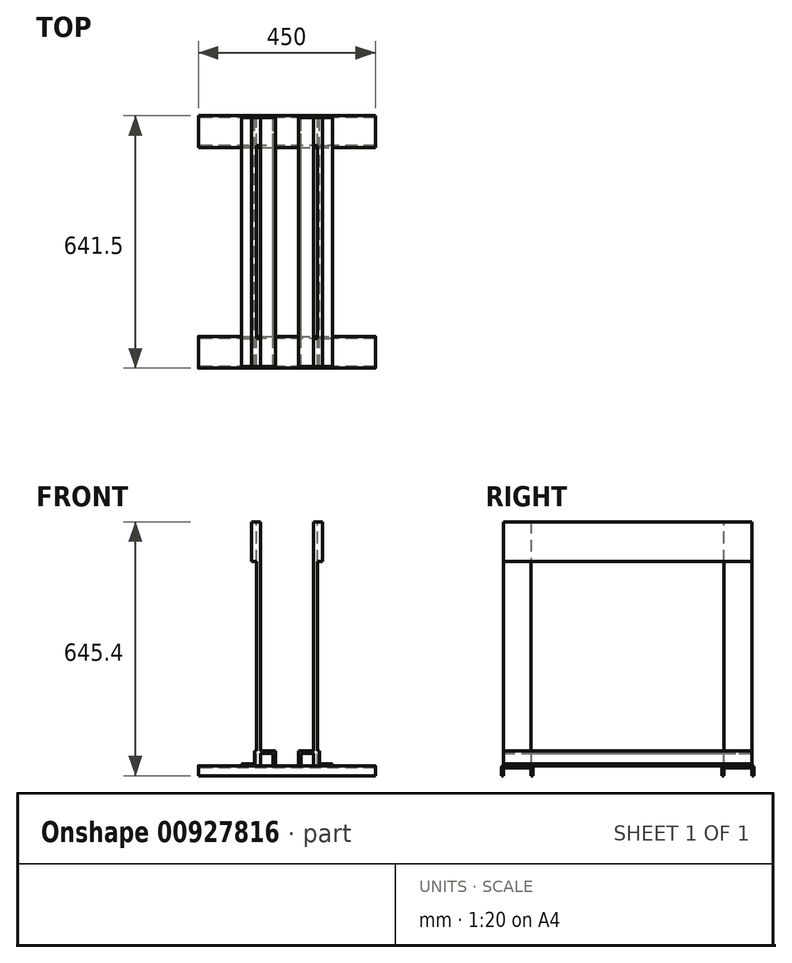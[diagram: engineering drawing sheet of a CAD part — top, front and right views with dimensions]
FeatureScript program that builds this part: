
annotation { "Feature Type Name" : "Feature", "Feature Type Description" : "" }
export const myFeature = defineFeature(function(context is Context, id is Id, definition is map)
    precondition{}
    {
        {
            var Q0;
            Q0=qCreatedBy(makeId("Front.planeOp"),FACE);
            var sketch = newSketch(context, id + "F0", { "sketchPlane" : qUnion([Q0])});
            skLineSegment(sketch, "E0.bottom", {"start": v(0, 0) * mm, "end": v(-10.45, 0) * mm});
            skLineSegment(sketch, "E0.top", {"start": v(0, 620) * mm, "end": v(-10.45, 620) * mm});
            skLineSegment(sketch, "E0.left", {"start": v(0, 0) * mm, "end": v(0, 620) * mm});
            skLineSegment(sketch, "E0.right", {"start": v(-10.45, 0) * mm, "end": v(-10.45, 620) * mm});
            skLineSegment(sketch, "E1", {"start": v(0, 38.1) * mm, "end": v(38.1, 38.1) * mm});
            skLineSegment(sketch, "E2", {"start": v(38.1, 38.1) * mm, "end": v(38.1, 0) * mm});
            skLineSegment(sketch, "E3", {"start": v(38.1, 0) * mm, "end": v(31.75, 0) * mm});
            skLineSegment(sketch, "E4", {"start": v(31.75, 0) * mm, "end": v(31.75, 31.75) * mm});
            skLineSegment(sketch, "E5", {"start": v(31.75, 31.75) * mm, "end": v(0, 31.75) * mm});
            skSolve(sketch);
        }
        {
            var Q0;
            {var subQ0=sQuery(id+"F0.wireOp",EDGE,"E1");Q0=makeQuery(id+"F0.imprint","IMPRINT",FACE,{"disambiguationData":[TD([[makeQuery(id+"F0.imprint","IMPRINT",EDGE,{"derivedFrom":subQ0}),-1.0]])]});}
            extrude(context, id + "F1", {"entities" : qUnion([Q0]), "depth" : 631.5 * mm, "offsetDistance" : 25 * mm});
        }
        {
            var Q0;
            {var subQ3=sQuery(id+"F0.wireOp",EDGE,"E0.bottom");Q0=makeQuery(id+"F0.imprint","IMPRINT",FACE,{"disambiguationData":[TD([[makeQuery(id+"F0.imprint","IMPRINT",EDGE,{"derivedFrom":subQ3}),-1.0]])]});}
            extrude(context, id + "F2", {"entities" : qUnion([Q0]), "operationType" : NewBodyOperationType.ADD, "depth" : 70.75 * mm, "offsetDistance" : 25 * mm});
        }
        {
            var Q0;
            Q0=qCreatedBy(makeId("Top.planeOp"),FACE);
            var sketch = newSketch(context, id + "F3", { "sketchPlane" : qUnion([Q0])});
            skLineSegment(sketch, "E6.bottom", {"start": v(0, -631.5) * mm, "end": v(-10.45, -631.5) * mm});
            skLineSegment(sketch, "E6.top", {"start": v(0, -560.75) * mm, "end": v(-10.45, -560.75) * mm});
            skLineSegment(sketch, "E6.left", {"start": v(0, -631.5) * mm, "end": v(0, -560.75) * mm});
            skLineSegment(sketch, "E6.right", {"start": v(-10.45, -631.5) * mm, "end": v(-10.45, -560.75) * mm});
            skSolve(sketch);
        }
        {
            var Q0;
            Q0=qSketchRegion(id+"F3",true);
            extrude(context, id + "F4", {"entities" : qUnion([Q0]), "operationType" : NewBodyOperationType.ADD, "depth" : 620 * mm, "offsetDistance" : 25 * mm});
        }
        {
            var Q0;
            Q0=qCreatedBy(makeId("Top.planeOp"),FACE);
            var sketch = newSketch(context, id + "F5", { "sketchPlane" : qUnion([Q0])});
            skLineSegment(sketch, "E7.bottom", {"start": v(-157.8, 5) * mm, "end": v(292.2, 5) * mm});
            skLineSegment(sketch, "E7.top", {"start": v(-157.8, -75.75) * mm, "end": v(292.2, -75.75) * mm});
            skLineSegment(sketch, "E7.left", {"start": v(-157.8, 5) * mm, "end": v(-157.8, -75.75) * mm});
            skLineSegment(sketch, "E7.right", {"start": v(292.2, 5) * mm, "end": v(292.2, -75.75) * mm});
            skLineSegment(sketch, "E8.bottom", {"start": v(-157.8, -636.5) * mm, "end": v(292.2, -636.5) * mm});
            skLineSegment(sketch, "E8.top", {"start": v(-157.8, -555.75) * mm, "end": v(292.2, -555.75) * mm});
            skLineSegment(sketch, "E8.left", {"start": v(-157.8, -636.5) * mm, "end": v(-157.8, -555.75) * mm});
            skLineSegment(sketch, "E8.right", {"start": v(292.2, -636.5) * mm, "end": v(292.2, -555.75) * mm});
            skSolve(sketch);
        }
        {
            var Q0;
            Q0=qSketchRegion(id+"F5",true);
            extrude(context, id + "F6", {"entities" : qUnion([Q0]), "operationType" : NewBodyOperationType.ADD, "oppositeDirection" : true, "depth" : 25.4 * mm, "offsetDistance" : 25 * mm});
        }
        {
            var Q0;
            Q0=makeQuery(id+"F6.opExtrude","CAP_EDGE",EDGE,{"disambiguationData":[OSD([sQuery(id+"F5.wireOp",EDGE,"E8.bottom")])],"isStart":true});
            var Q1;
            {var subQ0=sQuery(id+"F5.wireOp",EDGE,"E8.top");var subQ1=makeQuery(id+"F6.opExtrude","SWEPT_FACE",FACE,{"disambiguationData":[OSD([subQ0])]});var subQ2=sQuery(id+"F5.wireOp",EDGE,"E8.right");var subQ3=makeQuery(id+"F6.opExtrude","CAP_FACE",FACE,{"disambiguationData":[OSD([sQuery(id+"F5.wireOp",EDGE,"E8.bottom"),subQ0,sQuery(id+"F5.wireOp",EDGE,"E8.left"),subQ2])],"isStart":true});Q1=makeQuery(id+"F6.boolean.opBoolean","SPLIT",EDGE,{"disambiguationData":[topologyDisambiguationEdgeConnected([subQ3,subQ1]),TD([makeQuery(id+"F1.opExtrude","SWEPT_FACE",FACE,{"disambiguationData":[OSD([sQuery(id+"F0.wireOp",EDGE,"E2")])]})])],"derivedFrom":makeQuery(id+"F6.opExtrude","CAP_EDGE",EDGE,{"disambiguationData":[OSD([subQ0])],"isStart":true})});}
            var Q2;
            {var subQ0=sQuery(id+"F5.wireOp",EDGE,"E8.top");var subQ1=makeQuery(id+"F6.opExtrude","SWEPT_FACE",FACE,{"disambiguationData":[OSD([subQ0])]});var subQ2=sQuery(id+"F5.wireOp",EDGE,"E8.left");var subQ3=makeQuery(id+"F6.opExtrude","CAP_FACE",FACE,{"disambiguationData":[OSD([sQuery(id+"F5.wireOp",EDGE,"E8.bottom"),subQ0,subQ2,sQuery(id+"F5.wireOp",EDGE,"E8.right")])],"isStart":true});Q2=makeQuery(id+"F6.boolean.opBoolean","SPLIT",EDGE,{"disambiguationData":[topologyDisambiguationEdgeConnected([subQ3,subQ1]),TD([makeQuery(id+"F1.opExtrude","SWEPT_FACE",FACE,{"disambiguationData":[OSD([sQuery(id+"F0.wireOp",EDGE,"E4")])]})])],"derivedFrom":makeQuery(id+"F6.opExtrude","CAP_EDGE",EDGE,{"disambiguationData":[OSD([subQ0])],"isStart":true})});}
            var Q3;
            {var subQ0=sQuery(id+"F5.wireOp",EDGE,"E7.top");var subQ1=makeQuery(id+"F6.opExtrude","SWEPT_FACE",FACE,{"disambiguationData":[OSD([subQ0])]});var subQ2=sQuery(id+"F5.wireOp",EDGE,"E7.right");var subQ3=makeQuery(id+"F6.opExtrude","CAP_FACE",FACE,{"disambiguationData":[OSD([sQuery(id+"F5.wireOp",EDGE,"E7.bottom"),subQ0,sQuery(id+"F5.wireOp",EDGE,"E7.left"),subQ2])],"isStart":true});Q3=makeQuery(id+"F6.boolean.opBoolean","SPLIT",EDGE,{"disambiguationData":[topologyDisambiguationEdgeConnected([subQ3,subQ1]),TD([makeQuery(id+"F1.opExtrude","SWEPT_FACE",FACE,{"disambiguationData":[OSD([sQuery(id+"F0.wireOp",EDGE,"E2")])]})])],"derivedFrom":makeQuery(id+"F6.opExtrude","CAP_EDGE",EDGE,{"disambiguationData":[OSD([subQ0])],"isStart":true})});}
            var Q4;
            {var subQ0=sQuery(id+"F5.wireOp",EDGE,"E7.top");var subQ1=makeQuery(id+"F6.opExtrude","SWEPT_FACE",FACE,{"disambiguationData":[OSD([subQ0])]});var subQ2=sQuery(id+"F5.wireOp",EDGE,"E7.left");var subQ3=makeQuery(id+"F6.opExtrude","CAP_FACE",FACE,{"disambiguationData":[OSD([sQuery(id+"F5.wireOp",EDGE,"E7.bottom"),subQ0,subQ2,sQuery(id+"F5.wireOp",EDGE,"E7.right")])],"isStart":true});Q4=makeQuery(id+"F6.boolean.opBoolean","SPLIT",EDGE,{"disambiguationData":[topologyDisambiguationEdgeConnected([subQ3,subQ1]),TD([makeQuery(id+"F1.opExtrude","SWEPT_FACE",FACE,{"disambiguationData":[OSD([sQuery(id+"F0.wireOp",EDGE,"E4")])]})])],"derivedFrom":makeQuery(id+"F6.opExtrude","CAP_EDGE",EDGE,{"disambiguationData":[OSD([subQ0])],"isStart":true})});}
            var Q5;
            Q5=makeQuery(id+"F6.opExtrude","CAP_EDGE",EDGE,{"disambiguationData":[OSD([sQuery(id+"F5.wireOp",EDGE,"E7.bottom")])],"isStart":true});
            fillet(context, id + "F7", {"entities" : qUnion([Q0, Q1, Q2, Q3, Q4, Q5]), "radius" : 5 * mm, "tangentPropagation" : true, "allowEdgeOverflow" : false});
        }
        {
            var Q0;
            Q0=qCreatedBy(makeId("Front.planeOp"),FACE);
            var sketch = newSketch(context, id + "F8", { "sketchPlane" : qUnion([Q0])});
            skLineSegment(sketch, "E9.bottom", {"start": v(134.4, 0) * mm, "end": v(144.85, 0) * mm});
            skLineSegment(sketch, "E9.top", {"start": v(134.4, 620) * mm, "end": v(144.85, 620) * mm});
            skLineSegment(sketch, "E9.left", {"start": v(134.4, 0) * mm, "end": v(134.4, 620) * mm});
            skLineSegment(sketch, "E9.right", {"start": v(144.85, 0) * mm, "end": v(144.85, 620) * mm});
            skLineSegment(sketch, "E10", {"start": v(134.4, 38.1) * mm, "end": v(96.3, 38.1) * mm});
            skLineSegment(sketch, "E11", {"start": v(96.3, 38.1) * mm, "end": v(96.3, 0) * mm});
            skLineSegment(sketch, "E12", {"start": v(96.3, 0) * mm, "end": v(102.65, 0) * mm});
            skLineSegment(sketch, "E13", {"start": v(102.65, 0) * mm, "end": v(102.65, 31.75) * mm});
            skLineSegment(sketch, "E14", {"start": v(102.65, 31.75) * mm, "end": v(134.4, 31.75) * mm});
            skSolve(sketch);
        }
        {
            var Q0;
            {var subQ0=sQuery(id+"F8.wireOp",EDGE,"E10");Q0=makeQuery(id+"F8.imprint","IMPRINT",FACE,{"disambiguationData":[TD([[makeQuery(id+"F8.imprint","IMPRINT",EDGE,{"derivedFrom":subQ0}),1.0]])]});}
            extrude(context, id + "F9", {"entities" : qUnion([Q0]), "operationType" : NewBodyOperationType.ADD, "depth" : 631.5 * mm, "offsetDistance" : 25 * mm});
        }
        {
            var Q0;
            Q0=qSketchRegion(id+"F8",true);
            extrude(context, id + "F10", {"entities" : qUnion([Q0]), "operationType" : NewBodyOperationType.ADD, "depth" : 70.75 * mm, "offsetDistance" : 25 * mm});
        }
        {
            var Q0;
            Q0=qCreatedBy(makeId("Top.planeOp"),FACE);
            var sketch = newSketch(context, id + "F11", { "sketchPlane" : qUnion([Q0])});
            skLineSegment(sketch, "E15.bottom", {"start": v(134.4, -631.5) * mm, "end": v(144.85, -631.5) * mm});
            skLineSegment(sketch, "E15.top", {"start": v(134.4, -560.75) * mm, "end": v(144.85, -560.75) * mm});
            skLineSegment(sketch, "E15.left", {"start": v(134.4, -631.5) * mm, "end": v(134.4, -560.75) * mm});
            skLineSegment(sketch, "E15.right", {"start": v(144.85, -631.5) * mm, "end": v(144.85, -560.75) * mm});
            skSolve(sketch);
        }
        {
            var Q0;
            Q0=qSketchRegion(id+"F11",true);
            extrude(context, id + "F12", {"entities" : qUnion([Q0]), "operationType" : NewBodyOperationType.ADD, "depth" : 620 * mm, "offsetDistance" : 25 * mm});
        }
        {
            var Q0;
            Q0=qCreatedBy(makeId("Front.planeOp"),FACE);
            var sketch = newSketch(context, id + "F13", { "sketchPlane" : qUnion([Q0])});
            skLineSegment(sketch, "E16.bottom", {"start": v(-10.45, 620) * mm, "end": v(-23.2, 620) * mm});
            skLineSegment(sketch, "E16.top", {"start": v(-10.45, 518.8) * mm, "end": v(-23.2, 518.8) * mm});
            skLineSegment(sketch, "E16.left", {"start": v(-10.45, 620) * mm, "end": v(-10.45, 518.8) * mm});
            skLineSegment(sketch, "E16.right", {"start": v(-23.2, 620) * mm, "end": v(-23.2, 518.8) * mm});
            skLineSegment(sketch, "E17.1.0.0", {"start": v(157.6, 620) * mm, "end": v(144.85, 620) * mm});
            skLineSegment(sketch, "E17.1.0.1", {"start": v(144.85, 620) * mm, "end": v(144.85, 518.8) * mm});
            skLineSegment(sketch, "E17.1.0.2", {"start": v(157.6, 518.8) * mm, "end": v(144.85, 518.8) * mm});
            skLineSegment(sketch, "E17.1.0.3", {"start": v(157.6, 620) * mm, "end": v(157.6, 518.8) * mm});
            skLineSegment(sketch, "E17.direction1", {"start": v(-23.2, 620) * mm, "end": v(144.85, 620) * mm, "construction": true});
            skSolve(sketch);
        }
        {
            var Q0;
            Q0=qSketchRegion(id+"F13",true);
            extrude(context, id + "F14", {"entities" : qUnion([Q0]), "operationType" : NewBodyOperationType.ADD, "depth" : 631.5 * mm, "offsetDistance" : 25 * mm});
        }
        {
            var Q0;
            Q0=qCreatedBy(makeId("Front.planeOp"),FACE);
            var sketch = newSketch(context, id + "F15", { "sketchPlane" : qUnion([Q0])});
            skLineSegment(sketch, "E18", {"start": v(-48.55, 0) * mm, "end": v(-10.45, 0) * mm});
            skLineSegment(sketch, "E19", {"start": v(-10.45, 0) * mm, "end": v(-10.45, 38.1) * mm});
            skLineSegment(sketch, "E20", {"start": v(-10.45, 38.1) * mm, "end": v(-15.21, 38.1) * mm});
            skLineSegment(sketch, "E21", {"start": v(-15.21, 38.1) * mm, "end": v(-15.21, 4.76) * mm});
            skLineSegment(sketch, "E22", {"start": v(-15.21, 4.76) * mm, "end": v(-48.55, 4.76) * mm});
            skLineSegment(sketch, "E23", {"start": v(-48.55, 4.76) * mm, "end": v(-48.55, 0) * mm});
            skLineSegment(sketch, "E24", {"start": v(182.95, 0) * mm, "end": v(144.85, 0) * mm});
            skLineSegment(sketch, "E25", {"start": v(144.85, 0) * mm, "end": v(144.85, 38.1) * mm});
            skLineSegment(sketch, "E26", {"start": v(144.85, 38.1) * mm, "end": v(149.61, 38.1) * mm});
            skLineSegment(sketch, "E27", {"start": v(149.61, 38.1) * mm, "end": v(149.61, 4.76) * mm});
            skLineSegment(sketch, "E28", {"start": v(149.61, 4.76) * mm, "end": v(182.95, 4.76) * mm});
            skLineSegment(sketch, "E29", {"start": v(182.95, 4.76) * mm, "end": v(182.95, 0) * mm});
            skSolve(sketch);
        }
        {
            var Q0;
            Q0=qSketchRegion(id+"F15",true);
            extrude(context, id + "F16", {"entities" : qUnion([Q0]), "operationType" : NewBodyOperationType.ADD, "depth" : 631.5 * mm, "offsetDistance" : 25 * mm});
        }
        {
            var Q0;
            Q0=qCreatedBy(makeId("Right.planeOp"),FACE);
            var sketch = newSketch(context, id + "F17", { "sketchPlane" : qUnion([Q0])});
            skLineSegment(sketch, "E30.bottom", {"start": v(-631.5, -25.4) * mm, "end": v(-560.75, -25.4) * mm});
            skLineSegment(sketch, "E30.top", {"start": v(-626.5, -5) * mm, "end": v(-565.75, -5) * mm});
            skLineSegment(sketch, "E30.left", {"start": v(-631.5, -25.4) * mm, "end": v(-631.5, -10) * mm});
            skLineSegment(sketch, "E30.right", {"start": v(-560.75, -25.4) * mm, "end": v(-560.75, -10) * mm});
            skPoint(sketch, "E31.visualSharp", {"position": v(-631.5, -5) * mm});
            skArc(sketch, "E31.filletArc", {"start": v(-626.5, -5) * mm, "mid": v(-630.04, -6.46) * mm, "end": v(-631.5, -10) * mm});
            skPoint(sketch, "E32.visualSharp", {"position": v(-560.75, -5) * mm});
            skArc(sketch, "E32.filletArc", {"start": v(-560.75, -10) * mm, "mid": v(-562.21, -6.46) * mm, "end": v(-565.75, -5) * mm});
            skArc(sketch, "E33.1.0.0", {"start": v(-65.75, -5) * mm, "mid": v(-69.29, -6.46) * mm, "end": v(-70.75, -10) * mm});
            skLineSegment(sketch, "E33.1.0.1", {"start": v(-70.75, -25.4) * mm, "end": v(-70.75, -10) * mm});
            skLineSegment(sketch, "E33.1.0.2", {"start": v(-70.75, -25.4) * mm, "end": v(0, -25.4) * mm});
            skLineSegment(sketch, "E33.1.0.3", {"start": v(0, -25.4) * mm, "end": v(0, -10) * mm});
            skArc(sketch, "E33.1.0.4", {"start": v(0, -10) * mm, "mid": v(-1.46, -6.46) * mm, "end": v(-5, -5) * mm});
            skLineSegment(sketch, "E33.1.0.5", {"start": v(-65.75, -5) * mm, "end": v(-5, -5) * mm});
            skLineSegment(sketch, "E33.direction1", {"start": v(-631.5, -10) * mm, "end": v(-70.75, -10) * mm, "construction": true});
            skSolve(sketch);
        }
        {
            var Q0;
            Q0=qSketchRegion(id+"F17",true);
            extrude(context, id + "F18", {"entities" : qUnion([Q0]), "operationType" : NewBodyOperationType.REMOVE, "depth" : 300 * mm, "offsetDistance" : 25 * mm});
        }
        {
            var Q0;
            Q0=qSketchRegion(id+"F17",true);
            extrude(context, id + "F19", {"entities" : qUnion([Q0]), "operationType" : NewBodyOperationType.REMOVE, "oppositeDirection" : true, "depth" : 300 * mm, "offsetDistance" : 25 * mm});
        }
    });
